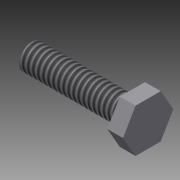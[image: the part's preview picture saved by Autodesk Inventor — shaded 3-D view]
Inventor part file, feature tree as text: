
AUTODESK INVENTOR PART (.ipt)
format: ipt  version: 2015 (Build 190159000, 159)  size: 89,088 bytes
history: native  units: in
note: dims shown in document units (in); Inventor stores cm internally (conversion verified against a paired STEP export)
features: extrude x2, sketch x2, thread x1
ambient origin geometry x8: Origin, YZ Plane, XZ Plane, XY Plane, X Axis, Y Axis, Z Axis, Center Point
bodies: Solid1 (feature_tree)
feature tree (5):
  extrude  "Extrusion1"  Depth=1.0in TaperAngle=0.0deg
  thread  "Thread1"  [1 undecoded]
  extrude  "Extrusion2"  Depth=0.1562in TaperAngle=0.0deg
  sketch  "Sketch1"  dims[d0=0.25in d1=1.0in d2=0.0in d3=1.0in d4=0.0in]
  sketch  "Sketch2"  dims[d5=0.5in d6=0.1562in d7=0.0in]
note: 1 required parameter value undecoded (feature->parameter linkage not recoverable at this tier; creation-order binding heuristic only, values carry confidence <= 0.55)
